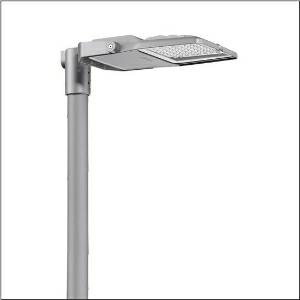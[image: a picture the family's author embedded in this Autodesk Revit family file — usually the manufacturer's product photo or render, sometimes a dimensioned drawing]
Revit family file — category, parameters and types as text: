
# Revit family: floodlight_fl_21_iq_mini___pl52_5xa7772c2d3a_4b1a
name_source: partatom
category: Lighting Fixtures
units: mm (PartAtom-declared; Revit-internal decimal feet)

## family parameters
Cut with Voids When Loaded = No
Host = Face
Light Source = No
Part Type = Normal
Room Calculation Point = No
Round Connector Dimension = Use Diameter
Shared = No

## types (1)
- --- (1 x LED, 12210 lm, 87.2 W, 3000K)
    Apparent Load = 87 VA
    CIE Flux Codes = 26 60 98 100 100
    Color Rendering = 70
    Color Temperature = 3000K
    Default Elevation = 1800 mm
    Description = Floodlight FL 21 iQ mini, floodlight, primary light control with lens, of PMMA, primary optical cover: protective disc, of toughened safety glass, transparent, light distribution: PL52, light emission: direct distribution, installation type: surface-mounted, LED, High Power LED, rated luminous flux: 12.210lm, luminous efficacy: 140lm/W, light colour: 730, colour temperature: 3000K, control gear: iQ Street-Remote/DALI, control: Auto-Match, Temp-Guard, Night-Set, Smart-Wire, Desk-Remote (wireless, voltage-free reading and setting of iQ features in the workshop via application-optimized NFC function/RFID function), optimised constant luminous flux control (CLO 2.0), Light-Fading, Lumen-Switch, with terminal, 6-pole, mains connection: 220..240V, AC, 50/60Hz, start of lifetime: 87W, end of service life: 92W, reduction: 40W, luminaire housing, of diecast aluminium, powder-coated, Siteco® metallic grey (DB 702S), corrosivity category C5 mid according to DIN EN ISO 12944, suitable for swimming pools, chlorine-resistant, sealing non-destructively replaceable, please order mast flange separately, mast bracket, of steel, galvanised, powder-coated, protection rating (complete): IP66, insulation class (complete): insulation class II (safety insulation), certification: CE, ENEC, VDE, protection symbol: D, impact resistance: IK08, permissible operating ambient temperature: -40..+40°C, permissible operating ambient temperature for outdoor applications: -40..+50°C, standard: DIN EN 12944, LABS conformity tested according to VDMA 24364:2018-05, packaging unit: 1 piece

Light Distribution: PL52
    Height = 70 mm
    Lamp = 1 x LED
    Lamp Light Flux = 12210 lm
    Lamp Power = 87.2 W
    Lamp count = 1
    Length = 485 mm
    Luminous efficacy = 140 lm/W
    Manufacturer = Siteco
    ModVariant = No
    Model = 5XA7772C2D3A
    Number of Poles = 1
    OnlyDefault = Yes
    Power Factor = 1
    Product Name = Floodlight FL 21 iQ mini | PL52
    Product group = floodlight | pylon annexe
    ProductGroupID = 6201
    Protection Class = Protection class II
    Protection Degree = IP 66
    RLX_Detail_Level = 1
    RLX_Emergency_Light_Flux = 0 lm
    RLX_Emergency_Type = 0
    RLX_Emergency_Type_DB = No
    RlxData = <blob elided: 101633 chars, md5=3a6bd643>
    Socket = socket
    Standby Power = 0 W
    System Light Flux = 12210 lm
    System Power = 87 W
    Type Comments = factory setting: luminous flux: 100 % | dim-lin: 254 | 456 mA
    Type Image = l_1007125.jpg
    URL = http://relux.com
    VarID = @adj_185761
    Voltage = 0 V
    Weight = 0.00 kg
    Width = 337 mm

## geometry (parser evidence)
native form markers: Blend x4, Sweep x11
no freeform markers — native parametric forms only
